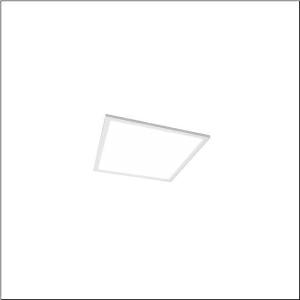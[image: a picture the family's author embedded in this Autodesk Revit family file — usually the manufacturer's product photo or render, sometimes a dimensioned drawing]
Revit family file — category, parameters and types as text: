
# Revit family: apollon_r__21_square_51mq13wd2313_d027
name_source: partatom
category: Lighting Fixtures
units: mm (PartAtom-declared; Revit-internal decimal feet)

## family parameters
Cut with Voids When Loaded = No
Host = Face
Light Source = No
Part Type = Normal
Room Calculation Point = No
Round Connector Dimension = Use Diameter
Shared = No

## types (1)
- Apollon® 21 square (1 x LED, 1700 lm, 15 W, 3000K)
    Apparent Load = 15 VA
    CIE Flux Codes = 59 88 97 100 100
    Color Rendering = 80
    Color Temperature = 3000K
    Default Elevation = 1800 mm
    Description = Apollon® 21 square, office luminaire, primary optical cover: micro prismatic cover, of PMMA, CAT 2 (L<= 3000cd/m²), light emission: direct distribution, primary light characteristic: symmetric, installation type: lay-in mounting, LED, rated luminous flux: 1.700lm, luminous efficacy: 113lm/W, light colour: 830, colour temperature: 3000K, control gear: ECG DALI, with terminal, 5-pole, mains connection: 220..240V, AC, 50/60Hz, rated input power: 15W, housing, of sheet steel, coated, pure white, length: 296mm, width: 296mm, height: 40mm, housing upper side, of sheet steel, galvanised, protection rating (complete): IP20, protection rating (lamp compartment, on room side): IP50, insulation class (complete): insulation class II (safety insulation), certification: CE, ENEC, permissible operating ambient temperature: -20..+40°C, packaging unit: 1 piece
    Height = 0 mm  [stored 0 ft]
    Lamp = 1 x LED
    Lamp Light Flux = 1700 lm
    Lamp Power = 15 W
    Lamp count = 1
    Length = 295 mm
    Luminous efficacy = 113 lm/W
    Manufacturer = Siteco
    ModVariant = No
    Model = 51MQ13WD2313
    Mounting Place = Ceiling
    Mounting Type = Recessed
    Number of Poles = 1
    OnlyDefault = Yes
    Power Factor = 1
    Product Name = Apollon® 21 square
    Product group = office luminaire | ceiling recessed
    ProductGroupID = 400
    Protection Class = Protection class II
    Protection Degree = IP 20
    RLX_Detail_Level = 1
    RLX_Emergency_Light_Flux = 0 lm
    RLX_Emergency_Type = 0
    RLX_Emergency_Type_DB = No
    RlxData = <blob elided: 10745 chars, md5=eddca93e>
    Socket = socket
    Standby Power = 0 W
    System Light Flux = 1700 lm
    System Power = 15 W
    Type Comments = Product without accessories
    Type Image = l_1291030.jpg
    URL = http://relux.com
    VarID = ---
    Voltage = 0 V
    Weight = 0.00 kg
    Width = 295 mm

note: [stored X ft] marks values corroborated as IEEE doubles in the binary element streams (Revit-internal decimal feet)

## geometry (parser evidence)
native form markers: Sweep x10
no freeform markers — native parametric forms only
